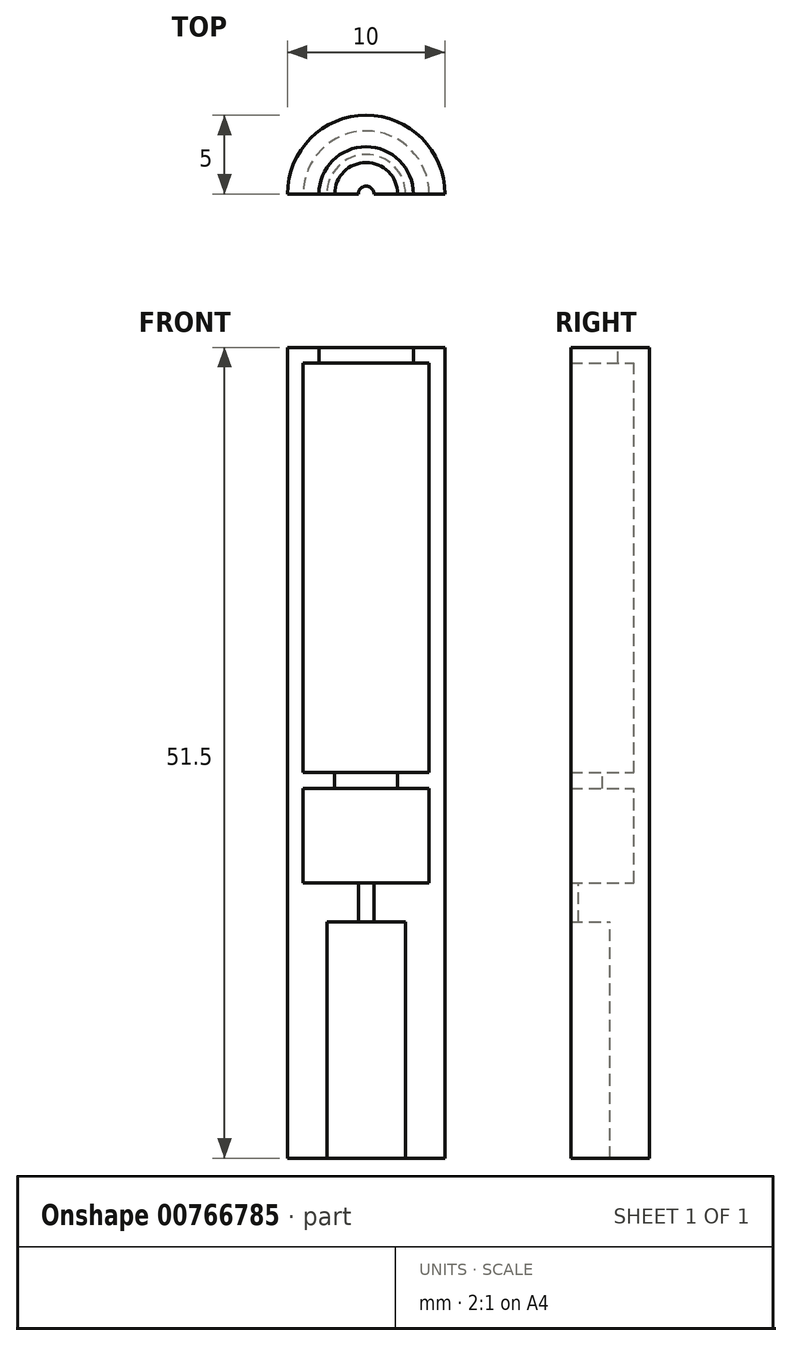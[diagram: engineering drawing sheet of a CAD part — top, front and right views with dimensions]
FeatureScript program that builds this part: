
annotation { "Feature Type Name" : "Feature", "Feature Type Description" : "" }
export const myFeature = defineFeature(function(context is Context, id is Id, definition is map)
    precondition{}
    {
        {
            var Q0;
            Q0=qCreatedBy(makeId("Front.planeOp"),FACE);
            var sketch = newSketch(context, id + "F0", { "sketchPlane" : qUnion([Q0])});
            skLineSegment(sketch, "E0", {"start": v(-3, 50.5) * mm, "end": v(-3, 51.5) * mm});
            skLineSegment(sketch, "E1", {"start": v(-3, 51.5) * mm, "end": v(-5, 51.5) * mm});
            skLineSegment(sketch, "E2", {"start": v(-5, 51.5) * mm, "end": v(-5, 0) * mm});
            skLineSegment(sketch, "E3", {"start": v(-3, 50.5) * mm, "end": v(-4, 50.5) * mm});
            skLineSegment(sketch, "E4", {"start": v(-4, 50.5) * mm, "end": v(-4, 24.5) * mm});
            skLineSegment(sketch, "E5", {"start": v(-4, 24.5) * mm, "end": v(-2, 24.5) * mm});
            skLineSegment(sketch, "E6", {"start": v(-2, 24.5) * mm, "end": v(-2, 23.5) * mm});
            skLineSegment(sketch, "E7", {"start": v(-2, 23.5) * mm, "end": v(-4, 23.5) * mm});
            skLineSegment(sketch, "E8", {"start": v(-4, 23.5) * mm, "end": v(-4, 17.5) * mm});
            skLineSegment(sketch, "E9", {"start": v(-4, 17.5) * mm, "end": v(-0.5, 17.5) * mm});
            skLineSegment(sketch, "E10", {"start": v(0, 30) * mm, "end": v(0, 0) * mm});
            skLineSegment(sketch, "E11", {"start": v(-0.5, 17.5) * mm, "end": v(-0.5, 15) * mm});
            skLineSegment(sketch, "E12", {"start": v(-0.5, 15) * mm, "end": v(-2.5, 15) * mm});
            skLineSegment(sketch, "E13", {"start": v(-2.5, 15) * mm, "end": v(-2.5, 0) * mm});
            skLineSegment(sketch, "E14", {"start": v(-2.5, 0) * mm, "end": v(-5, 0) * mm});
            skSolve(sketch);
        }
        {
            var Q0;
            Q0 = qSketchRegion(id + "F0", true);
            var Q1;
            Q1=sQuery(id+"F0.wireOp",EDGE,"E10");
            revolve(context, id + "F1", {"surfaceOperationType" : NewSurfaceOperationType.NEW, "entities" : qUnion([Q0]), "axis" : qUnion([Q1]), "revolveType" : RevolveType.ONE_DIRECTION, "angle" : 180 * degree});
        }
    });
